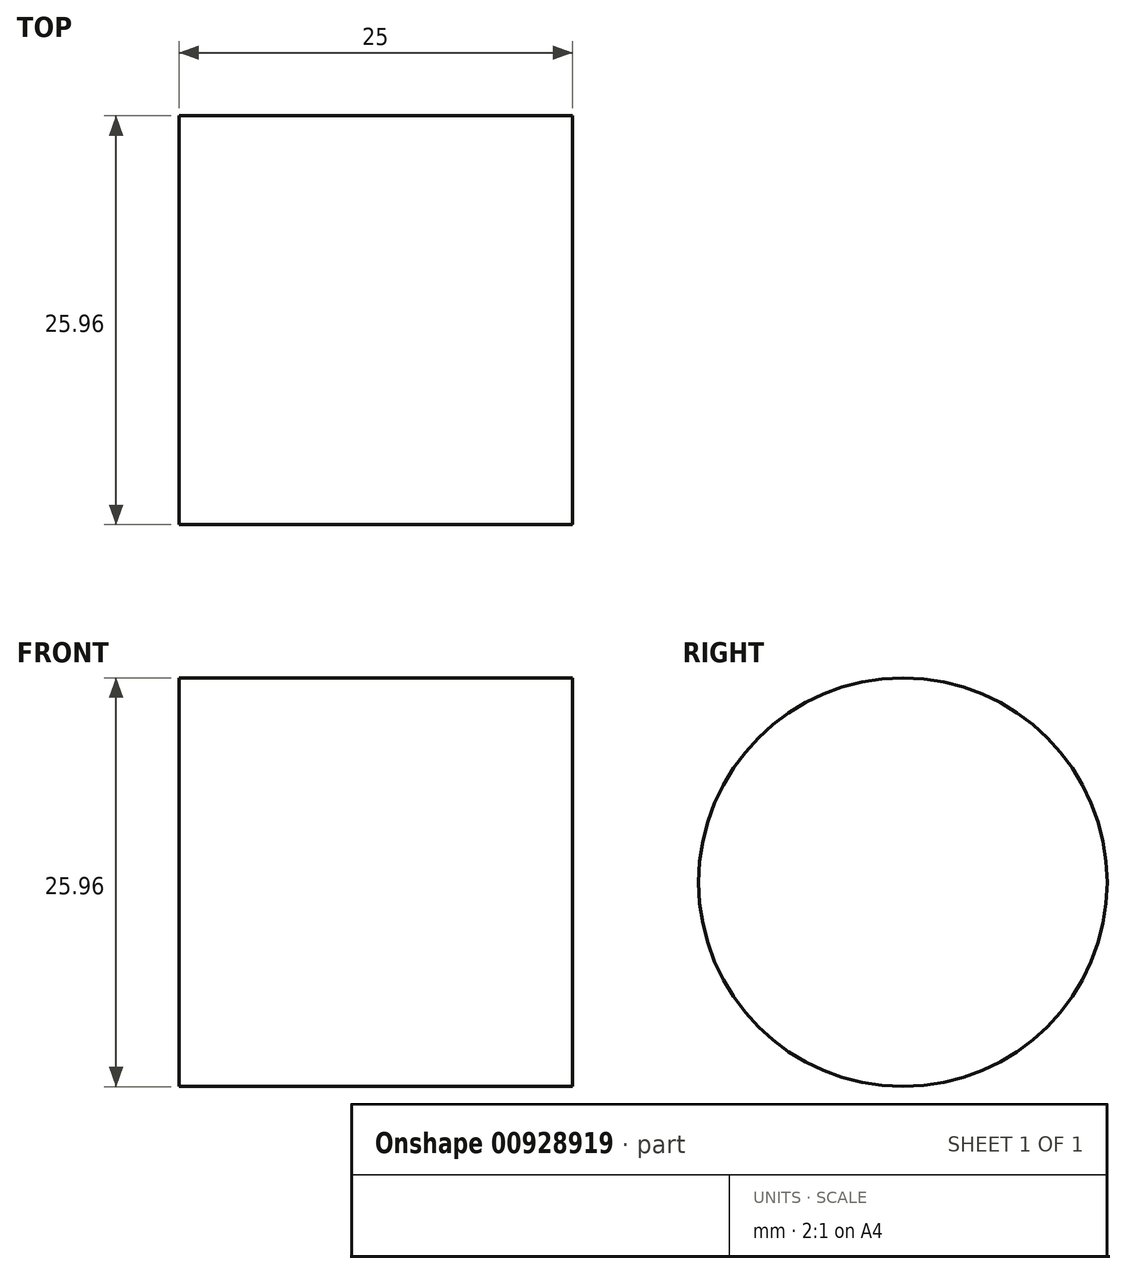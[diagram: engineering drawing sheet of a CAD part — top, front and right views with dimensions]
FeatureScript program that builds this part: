
annotation { "Feature Type Name" : "Feature", "Feature Type Description" : "" }
export const myFeature = defineFeature(function(context is Context, id is Id, definition is map)
    precondition{}
    {
        {
            var Q0;
            Q0=qCreatedBy(makeId("Front.planeOp"),FACE);
            var sketch = newSketch(context, id + "F0", { "sketchPlane" : qUnion([Q0])});
            skLineSegment(sketch, "E0", {"start": v(0, 0) * mm, "end": v(0, 12.97) * mm});
            skLineSegment(sketch, "E1", {"start": v(0, 12.97) * mm, "end": v(25, 12.97) * mm});
            skLineSegment(sketch, "E2", {"start": v(25, 12.97) * mm, "end": v(25, 0) * mm});
            skLineSegment(sketch, "E3", {"start": v(25, 0) * mm, "end": v(0, 0) * mm});
            skSolve(sketch);
        }
        {
            var Q0;
            Q0=makeQuery(id+"F0.imprint","IMPRINT",FACE,{"disambiguationData":[TD([[makeQuery(id+"F0.imprint","IMPRINT",EDGE,{"derivedFrom":sQuery(id+"F0.wireOp",EDGE,"E0")}),-1.0]])]});
            var Q1;
            Q1=sQuery(id+"F0.wireOp",EDGE,"E3");
            revolve(context, id + "F1", {"surfaceOperationType" : NewSurfaceOperationType.NEW, "entities" : qUnion([Q0]), "axis" : qUnion([Q1]), "revolveType" : RevolveType.FULL});
        }
    });
